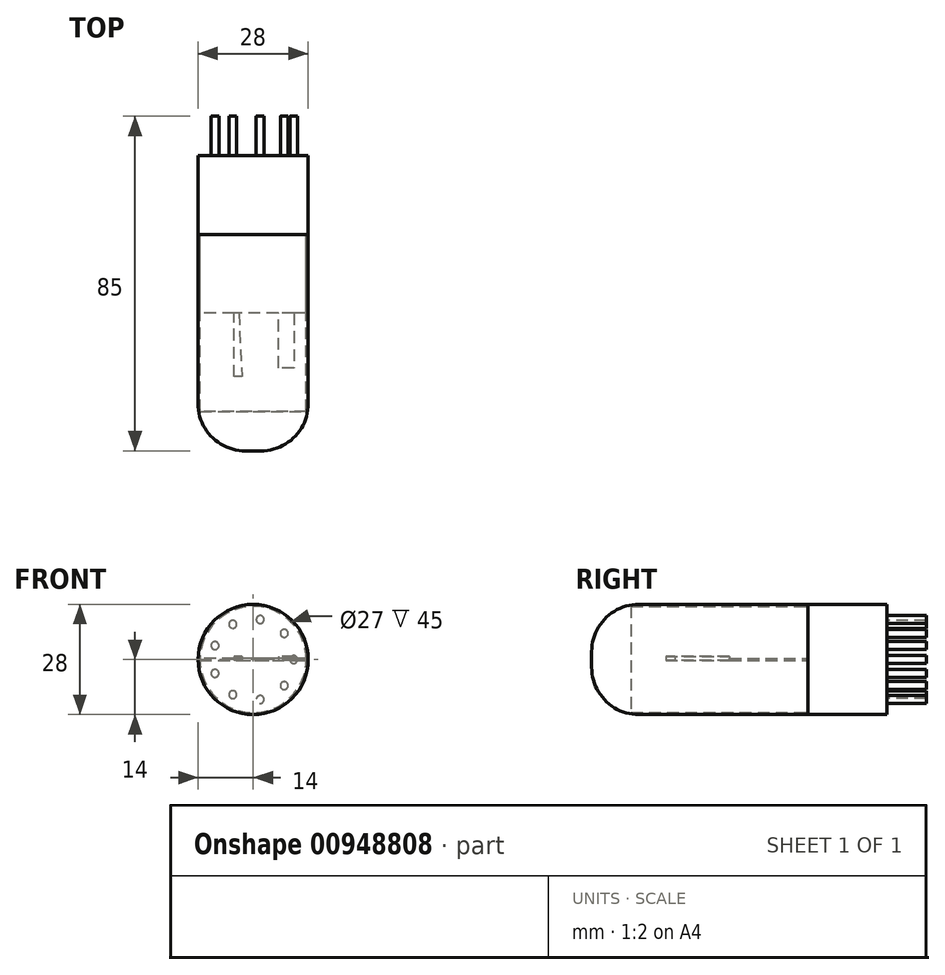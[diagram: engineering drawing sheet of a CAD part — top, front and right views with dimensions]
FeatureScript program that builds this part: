
annotation { "Feature Type Name" : "Feature", "Feature Type Description" : "" }
export const myFeature = defineFeature(function(context is Context, id is Id, definition is map)
    precondition{}
    {
        {
            var Q0;
            Q0=qCreatedBy(makeId("Front.planeOp"),FACE);
            var sketch = newSketch(context, id + "F0", { "sketchPlane" : qUnion([Q0])});
            skCircle(sketch, "E0", {"center": v(0, 0) * mm, "radius": 14 * mm});
            skSolve(sketch);
        }
        {
            var Q0;
            Q0 = qSketchRegion(id + "F0", true);
            extrude(context, id + "F1", {"entities" : qUnion([Q0]), "depth" : 25 * mm, "offsetDistance" : 25 * mm});
        }
        {
            var Q0;
            Q0 = qSketchRegion(id + "F0", true);
            extrude(context, id + "F2", {"entities" : qUnion([Q0]), "operationType" : NewBodyOperationType.ADD, "depth" : 55 * mm, "offsetDistance" : 25 * mm});
        }
        {
            var Q0;
            Q0=makeQuery(id+"F2.opExtrude","CAP_FACE",FACE,{"disambiguationData":[OSD([sQuery(id+"F0.wireOp",EDGE,"E0")])],"isStart":false});
            fillet(context, id + "F3", {"entities" : qUnion([Q0]), "radius" : 12 * mm, "tangentPropagation" : true, "allowEdgeOverflow" : false});
        }
        {
            var Q0;
            Q0=makeQuery(id+"F1.opExtrude","CAP_FACE",FACE,{"disambiguationData":[OSD([sQuery(id+"F0.wireOp",EDGE,"E0")])],"isStart":true});
            var sketch = newSketch(context, id + "F4", { "sketchPlane" : qUnion([Q0])});
            skCircle(sketch, "E1", {"center": v(0, 0) * mm, "radius": 13.5 * mm});
            skSolve(sketch);
        }
        {
            var Q0;
            Q0=makeQuery(id+"F4.imprint","IMPRINT",FACE,{"disambiguationData":[TD([[makeQuery(id+"F4.imprint","IMPRINT",EDGE,{"derivedFrom":sQuery(id+"F4.wireOp",EDGE,"E1")}),1.0]])]});
            extrude(context, id + "F5", {"entities" : qUnion([Q0]), "operationType" : NewBodyOperationType.REMOVE, "oppositeDirection" : true, "depth" : 45 * mm, "offsetDistance" : 25 * mm});
        }
        {
            var Q0;
            Q0=makeQuery(id+"F1.opExtrude","CAP_FACE",FACE,{"disambiguationData":[OSD([sQuery(id+"F0.wireOp",EDGE,"E0")])],"isStart":true});
            var sketch = newSketch(context, id + "F6", { "sketchPlane" : qUnion([Q0])});
            skLineSegment(sketch, "E2", {"start": v(-13.5, 0.25) * mm, "end": v(13.5, 0.25) * mm});
            skLineSegment(sketch, "E3", {"start": v(-12.06, -0.25) * mm, "end": v(-13.5, -0.25) * mm});
            skLineSegment(sketch, "E4", {"start": v(-13.5, -0.25) * mm, "end": v(-12.06, -0.25) * mm});
            skLineSegment(sketch, "E5", {"start": v(-12.06, -0.25) * mm, "end": v(13.5, -0.25) * mm});
            skSolve(sketch);
        }
        {
            var Q0;
            {var subQ2=sQuery(id+"F6.wireOp",EDGE,"E2");Q0=makeQuery(id+"F6.imprint","IMPRINT",FACE,{"disambiguationData":[TD([[makeQuery(id+"F6.imprint","IMPRINT",EDGE,{"derivedFrom":subQ2}),-1.0]])]});}
            extrude(context, id + "F7", {"entities" : qUnion([Q0]), "oppositeDirection" : true, "depth" : 20 * mm, "offsetDistance" : 25 * mm});
        }
        {
            var Q0;
            Q0=makeQuery(id+"F7.opExtrude","SWEPT_FACE",FACE,{"disambiguationData":[OSD([sQuery(id+"F6.wireOp",EDGE,"E2")])]});
            var sketch = newSketch(context, id + "F8", { "sketchPlane" : qUnion([Q0])});
            skLineSegment(sketch, "E6", {"start": v(10.4, -20) * mm, "end": v(10.4, -33.88) * mm});
            skLineSegment(sketch, "E7", {"start": v(10.4, -33.88) * mm, "end": v(6.4, -33.88) * mm});
            skLineSegment(sketch, "E8", {"start": v(6.4, -33.88) * mm, "end": v(6.4, -20) * mm});
            skLineSegment(sketch, "E9", {"start": v(-3.6, -20) * mm, "end": v(-2.88, -36.07) * mm});
            skLineSegment(sketch, "E10", {"start": v(-2.88, -36.07) * mm, "end": v(-4.8, -36.16) * mm});
            skLineSegment(sketch, "E11", {"start": v(-4.8, -36.16) * mm, "end": v(-4.8, -20) * mm});
            skLineSegment(sketch, "E12", {"start": v(6.4, -20) * mm, "end": v(10.4, -20) * mm});
            skLineSegment(sketch, "E13", {"start": v(-3.6, -20) * mm, "end": v(-4.8, -20) * mm});
            skSolve(sketch);
        }
        {
            var Q0;
            Q0 = qSketchRegion(id + "F8", true);
            extrude(context, id + "F9", {"entities" : qUnion([Q0]), "operationType" : NewBodyOperationType.ADD, "depth" : 1 * mm, "hasOffset" : true, "offsetDistance" : 25 * mm, "offsetOppositeDirection" : true, "symmetric" : true});
        }
        {
            var Q0;
            Q0=makeQuery(id+"F0.imprint","IMPRINT",FACE,{"disambiguationData":[TD([[makeQuery(id+"F0.imprint","IMPRINT",EDGE,{"derivedFrom":sQuery(id+"F0.wireOp",EDGE,"E0")}),1.0]])]});
            var sketch = newSketch(context, id + "F10", { "sketchPlane" : qUnion([Q0])});
            skCircle(sketch, "E14", {"center": v(0, 0) * mm, "radius": 14 * mm});
            skSolve(sketch);
        }
        {
            var Q0;
            Q0 = qSketchRegion(id + "F10", true);
            extrude(context, id + "F11", {"entities" : qUnion([Q0]), "oppositeDirection" : true, "depth" : 20 * mm, "offsetDistance" : 25 * mm});
        }
        {
            var Q0;
            Q0=makeQuery(id+"F11.opExtrude","CAP_FACE",FACE,{"disambiguationData":[OSD([sQuery(id+"F10.wireOp",EDGE,"E14")])],"isStart":false});
            var sketch = newSketch(context, id + "F12", { "sketchPlane" : qUnion([Q0])});
            skPoint(sketch, "E15.0.midPoint", {"position": v(9.69, 0) * mm});
            skCircle(sketch, "E16", {"center": v(-1.8, -10.15) * mm, "radius": 1 * mm});
            skCircle(sketch, "E17", {"center": v(5.16, -8.93) * mm, "radius": 1 * mm});
            skCircle(sketch, "E18", {"center": v(9.69, -3.53) * mm, "radius": 1 * mm});
            skCircle(sketch, "E19", {"center": v(9.69, 3.53) * mm, "radius": 1 * mm});
            skCircle(sketch, "E20", {"center": v(5.16, 8.93) * mm, "radius": 1 * mm});
            skCircle(sketch, "E21", {"center": v(-1.8, 10.15) * mm, "radius": 1 * mm});
            skCircle(sketch, "E22", {"center": v(-7.9, 6.63) * mm, "radius": 1 * mm});
            skCircle(sketch, "E23", {"center": v(-10.31, 0) * mm, "radius": 1 * mm});
            skCircle(sketch, "E24", {"center": v(-7.9, -6.63) * mm, "radius": 1 * mm});
            skSolve(sketch);
        }
        {
            var Q0;
            Q0=makeQuery(id+"F12.imprint","IMPRINT",FACE,{"disambiguationData":[TD([[makeQuery(id+"F12.imprint","IMPRINT",EDGE,{"derivedFrom":sQuery(id+"F12.wireOp",EDGE,"E17")}),1.0]])]});
            var Q1;
            Q1=makeQuery(id+"F12.imprint","IMPRINT",FACE,{"disambiguationData":[TD([[makeQuery(id+"F12.imprint","IMPRINT",EDGE,{"derivedFrom":sQuery(id+"F12.wireOp",EDGE,"E18")}),1.0]])]});
            var Q2;
            Q2=makeQuery(id+"F12.imprint","IMPRINT",FACE,{"disambiguationData":[TD([[makeQuery(id+"F12.imprint","IMPRINT",EDGE,{"derivedFrom":sQuery(id+"F12.wireOp",EDGE,"E19")}),1.0]])]});
            var Q3;
            Q3=makeQuery(id+"F12.imprint","IMPRINT",FACE,{"disambiguationData":[TD([[makeQuery(id+"F12.imprint","IMPRINT",EDGE,{"derivedFrom":sQuery(id+"F12.wireOp",EDGE,"E20")}),1.0]])]});
            var Q4;
            Q4=makeQuery(id+"F12.imprint","IMPRINT",FACE,{"disambiguationData":[TD([[makeQuery(id+"F12.imprint","IMPRINT",EDGE,{"derivedFrom":sQuery(id+"F12.wireOp",EDGE,"E21")}),1.0]])]});
            var Q5;
            Q5=makeQuery(id+"F12.imprint","IMPRINT",FACE,{"disambiguationData":[TD([[makeQuery(id+"F12.imprint","IMPRINT",EDGE,{"derivedFrom":sQuery(id+"F12.wireOp",EDGE,"E22")}),1.0]])]});
            var Q6;
            Q6=makeQuery(id+"F12.imprint","IMPRINT",FACE,{"disambiguationData":[TD([[makeQuery(id+"F12.imprint","IMPRINT",EDGE,{"derivedFrom":sQuery(id+"F12.wireOp",EDGE,"E23")}),1.0]])]});
            var Q7;
            Q7=makeQuery(id+"F12.imprint","IMPRINT",FACE,{"disambiguationData":[TD([[makeQuery(id+"F12.imprint","IMPRINT",EDGE,{"derivedFrom":sQuery(id+"F12.wireOp",EDGE,"E24")}),1.0]])]});
            var Q8;
            Q8=makeQuery(id+"F12.imprint","IMPRINT",FACE,{"disambiguationData":[TD([[makeQuery(id+"F12.imprint","IMPRINT",EDGE,{"derivedFrom":sQuery(id+"F12.wireOp",EDGE,"E16")}),1.0]])]});
            extrude(context, id + "F13", {"entities" : qUnion([Q0, Q1, Q2, Q3, Q4, Q5, Q6, Q7, Q8]), "operationType" : NewBodyOperationType.ADD, "depth" : 10 * mm, "offsetDistance" : 25 * mm});
        }
    });
